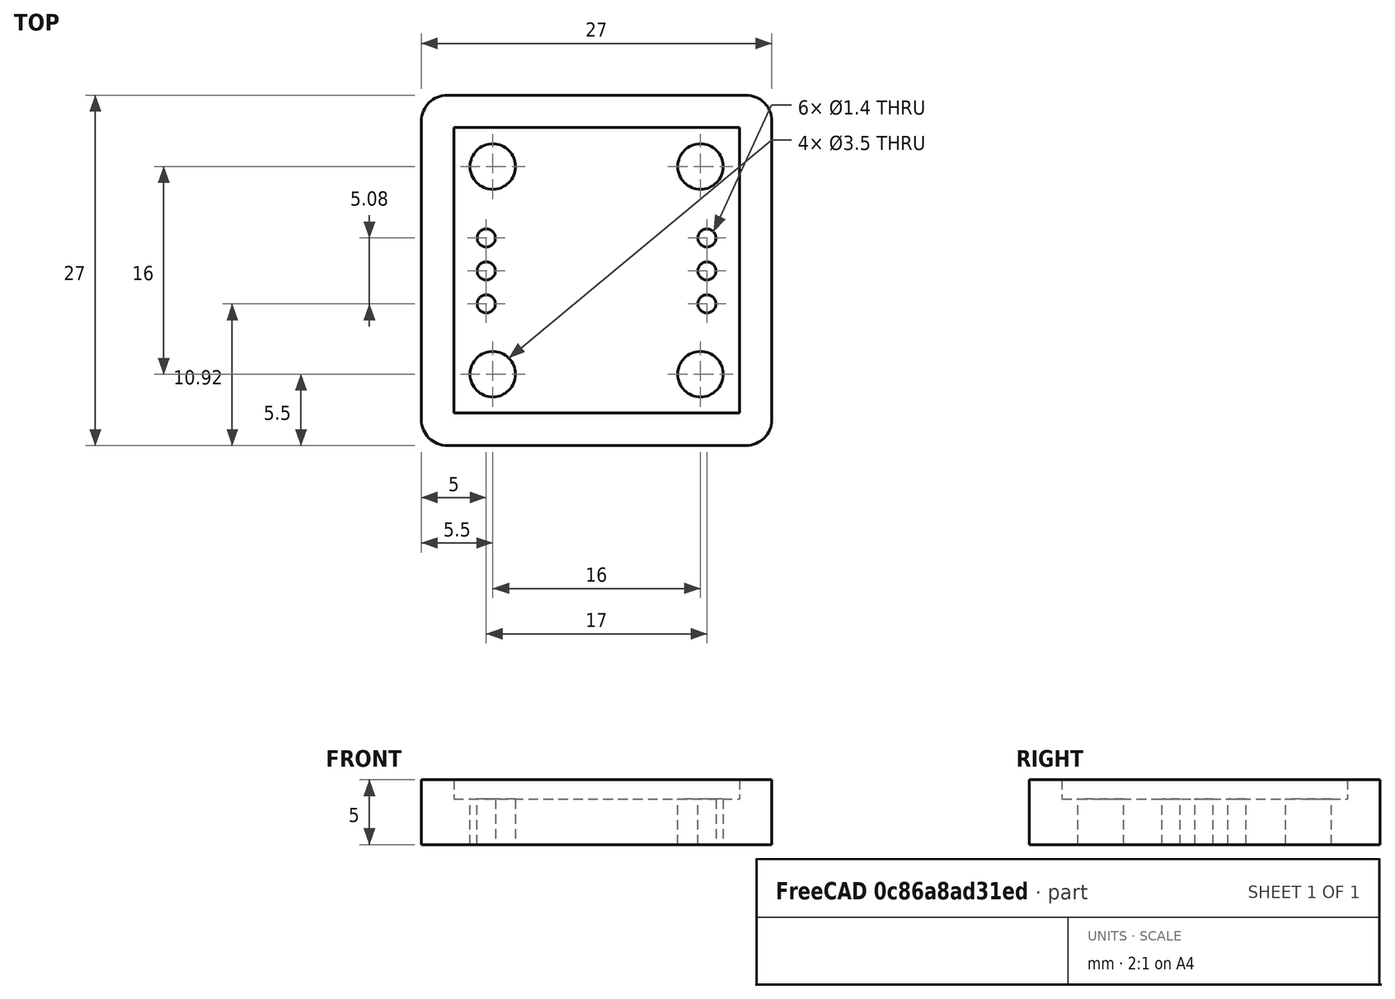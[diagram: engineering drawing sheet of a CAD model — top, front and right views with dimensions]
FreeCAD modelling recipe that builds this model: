
FCSTD DOCUMENT  (FreeCAD 1.1R44874 (Git))
Label: carrier1
Comment: Carrier for readout1
License: BSD 2-Clause
objects: Sketcher::SketchObject×4, PartDesign::Pocket×3, App::Point×1, PartDesign::Pad×1, PartDesign::Body×1, Mesh::Feature×1
note: 21 computed .brp shape members not serialized (recipe doc carries the construction recipe); baked Part::Feature solids carry a one-line shape summary decoded from their .brp

FEATURE [App::Point] Origin001
  Role = Origin
FEATURE [Sketcher::SketchObject] Sketch
  ArcFitTolerance = 1e-06
  AttachmentSupport = -> [Origin]
  ExternalTypes = [0]
  FullyConstrained = true
  MakeInternals = false
  MapMode = 5
  _ExternalGeoVersion = 1
  expr: Constraints[27] = .Constraints.outer - 2 * .Constraints.outerfilletradius
  sketch-geometry (13):
    g0: LineSegment StartX=-11.5 StartY=-13.5 StartZ=0 EndX=11.5 EndY=-13.5 EndZ=0
    g1: LineSegment StartX=13.5 StartY=-11.5 StartZ=0 EndX=13.5 EndY=11.5 EndZ=0
    g2: LineSegment StartX=11.5 StartY=13.5 StartZ=0 EndX=-11.5 EndY=13.5 EndZ=0
    g3: LineSegment StartX=-13.5 StartY=11.5 StartZ=0 EndX=-13.5 EndY=-11.5 EndZ=0
    g4: GeomPoint [constr] X=0 Y=0 Z=0
    g5: ArcOfCircle CenterX=-11.5 CenterY=11.5 CenterZ=0 NormalX=0 NormalY=0 NormalZ=1 AngleXU=0 Radius=2 StartAngle=1.5708 EndAngle=3.14159
    g6: GeomPoint [constr] X=-13.5 Y=13.5 Z=0
    g7: ArcOfCircle CenterX=-11.5 CenterY=-11.5 CenterZ=0 NormalX=0 NormalY=0 NormalZ=1 AngleXU=0 Radius=2 StartAngle=3.14159 EndAngle=4.71239
    g8: GeomPoint [constr] X=-13.5 Y=-13.5 Z=0
    g9: ArcOfCircle CenterX=11.5 CenterY=-11.5 CenterZ=0 NormalX=0 NormalY=0 NormalZ=1 AngleXU=0 Radius=2 StartAngle=4.71239 EndAngle=6.28319
    g10: GeomPoint [constr] X=13.5 Y=-13.5 Z=0
    g11: ArcOfCircle CenterX=11.5 CenterY=11.5 CenterZ=0 NormalX=0 NormalY=0 NormalZ=1 AngleXU=0 Radius=2 StartAngle=0 EndAngle=1.5708
    g12: GeomPoint [constr] X=13.5 Y=13.5 Z=0
  constraints (28):
    c: Horizontal(g0)
    c: Horizontal(g2)
    c: Vertical(g1)
    c: Vertical(g3)
    c: Symmetric(g12,g8,g4)
    c: Coincident(g4,g-1)
    c: DistanceX(g6,g12) = 27  'outer'
    c: PointOnObject(g6,g2)
    c: PointOnObject(g6,g3)
    c: Tangent(g2,g5) = -1.5708
    c: Tangent(g3,g5) = -1.5708
    c: PointOnObject(g8,g3)
    c: PointOnObject(g8,g0)
    c: Tangent(g3,g7) = -1.5708
    c: Tangent(g0,g7) = -1.5708
    c: PointOnObject(g10,g0)
    c: PointOnObject(g10,g1)
    c: Tangent(g0,g9) = -1.5708
    c: Tangent(g1,g9) = -1.5708
    c: PointOnObject(g12,g1)
    c: PointOnObject(g12,g2)
    c: Tangent(g1,g11) = -1.5708
    c: Tangent(g2,g11) = -1.5708
    c: Radius(g11) = 2  'outerfilletradius'
    c: Equal(g2,g3)
    c: Equal(g3,g0)
    c: Equal(g0,g1)
    c: DistanceX(g2,g2) = 23
FEATURE [PartDesign::Pad] Pad
  Direction = (0,0,1)
  Length = 5
  Length2 = 10
  Profile = -> Sketch
  ReferenceAxis = -> Sketch [N_Axis]
  Refine = true
  SideType = 0
  Suppressed = false
  Type = 0
  Type2 = 0
FEATURE [Sketcher::SketchObject] Sketch001
  ArcFitTolerance = 1e-06
  AttachmentSupport = -> [Pad]
  ExternalTypes = [0]
  FullyConstrained = true
  MakeInternals = false
  MapMode = 5
  Placement = pos=(0,0,5) rot=(0,0,1;0rad)
  _ExternalGeoVersion = 1
  sketch-geometry (5):
    g0: LineSegment StartX=-11 StartY=-11 StartZ=0 EndX=11 EndY=-11 EndZ=0
    g1: LineSegment StartX=11 StartY=-11 StartZ=0 EndX=11 EndY=11 EndZ=0
    g2: LineSegment StartX=11 StartY=11 StartZ=0 EndX=-11 EndY=11 EndZ=0
    g3: LineSegment StartX=-11 StartY=11 StartZ=0 EndX=-11 EndY=-11 EndZ=0
    g4: GeomPoint [constr] X=0 Y=0 Z=0
  constraints (12):
    c: Coincident(g0,g1)
    c: Coincident(g1,g2)
    c: Coincident(g2,g3)
    c: Coincident(g3,g0)
    c: Horizontal(g0)
    c: Horizontal(g2)
    c: Vertical(g1)
    c: Vertical(g3)
    c: Symmetric(g2,g0,g4)
    c: Coincident(g4,g-1)
    c: DistanceX(g2,g2) = 22  'outerpcb'
    c: Equal(g2,g3)
FEATURE [PartDesign::Pocket] Pocket  label="PCBPocket"
  BaseFeature = -> Pad
  Direction = (0,0,-1)
  Length = 1.5
  Length2 = 5
  Profile = -> Sketch001
  ReferenceAxis = -> Sketch001 [N_Axis]
  Refine = true
  SideType = 0
  Suppressed = false
  Type = 0
  Type2 = 0
FEATURE [Sketcher::SketchObject] Sketch002  label="mtgholes"
  ArcFitTolerance = 1e-06
  AttachmentSupport = -> [Pocket]
  ExternalTypes = [0]
  FullyConstrained = true
  MakeInternals = false
  MapMode = 5
  Placement = pos=(0,0,3.5) rot=(0,0,1;0rad)
  _ExternalGeoVersion = 1
  sketch-geometry (4):
    g0: Circle CenterX=8 CenterY=8 CenterZ=0 NormalX=0 NormalY=0 NormalZ=1 AngleXU=0 Radius=1.75
    g1: Circle CenterX=-8 CenterY=8 CenterZ=0 NormalX=0 NormalY=0 NormalZ=1 AngleXU=0 Radius=1.75
    g2: Circle CenterX=-8 CenterY=-8 CenterZ=0 NormalX=0 NormalY=0 NormalZ=1 AngleXU=0 Radius=1.75
    g3: Circle CenterX=8 CenterY=-8 CenterZ=0 NormalX=0 NormalY=0 NormalZ=1 AngleXU=0 Radius=1.75
  constraints (9):
    c: DistanceX(g-1,g0) = 8  'mtgholex'
    c: DistanceY(g-1,g0) = 8  'mtgholey'
    c: Equal(g0,g1)
    c: Equal(g0,g2)
    c: Equal(g0,g3)
    c: Symmetric(g1,g0,g-2)
    c: Symmetric(g3,g0,g-1)
    c: Symmetric(g2,g0,g-1)
    c: Diameter(g0) = 3.5  'mtgholedia'
FEATURE [PartDesign::Pocket] Pocket001
  BaseFeature = -> Pocket
  Direction = (0,0,-1)
  Length = 5
  Length2 = 5
  Profile = -> Sketch002
  ReferenceAxis = -> Sketch002 [N_Axis]
  Refine = true
  SideType = 0
  Suppressed = false
  Type = 2
  Type2 = 0
FEATURE [Sketcher::SketchObject] Sketch003
  ArcFitTolerance = 1e-06
  AttachmentSupport = -> [Pocket001]
  ExternalTypes = [0]
  FullyConstrained = true
  MakeInternals = false
  MapMode = 5
  Placement = pos=(0,0,3.5) rot=(0,0,1;0rad)
  _ExternalGeoVersion = 1
  sketch-geometry (6):
    g0: Circle CenterX=8.5 CenterY=2.5 CenterZ=0 NormalX=0 NormalY=0 NormalZ=1 AngleXU=0 Radius=0.7
    g1: Circle CenterX=8.5 CenterY=-0.04 CenterZ=0 NormalX=0 NormalY=0 NormalZ=1 AngleXU=0 Radius=0.7
    g2: Circle CenterX=8.5 CenterY=-2.58 CenterZ=0 NormalX=0 NormalY=0 NormalZ=1 AngleXU=0 Radius=0.7
    g3: Circle CenterX=-8.5 CenterY=2.5 CenterZ=0 NormalX=0 NormalY=0 NormalZ=1 AngleXU=0 Radius=0.7
    g4: Circle CenterX=-8.5 CenterY=-0.04 CenterZ=0 NormalX=0 NormalY=0 NormalZ=1 AngleXU=0 Radius=0.7
    g5: Circle CenterX=-8.5 CenterY=-2.58 CenterZ=0 NormalX=0 NormalY=0 NormalZ=1 AngleXU=0 Radius=0.7
  constraints (15):
    c: Diameter(g0) = 1.4  'pindia'
    c: DistanceX(g-1,g0) = 8.5  'pin1x'
    c: DistanceY(g-1,g0) = 2.5  'pin1y'
    c: Diameter(g4) = 1.4
    c: Equal(g5,g2)
    c: Equal(g2,g1)
    c: Symmetric(g5,g2,g-2)
    c: Symmetric(g4,g1,g-2)
    c: Symmetric(g3,g0,g-2)
    c: Equal(g4,g3)
    c: Equal(g1,g0)
    c: DistanceX(g-1,g2) = 8.5
    c: DistanceX(g-1,g1) = 8.5
    c: DistanceY(g2,g1) = 2.54
    c: DistanceY(g4,g3) = 2.54
FEATURE [PartDesign::Pocket] Pocket002
  BaseFeature = -> Pocket001
  Direction = (0,0,-1)
  Length = 5
  Length2 = 5
  Profile = -> Sketch003
  ReferenceAxis = -> Sketch003 [N_Axis]
  Refine = true
  SideType = 0
  Suppressed = false
  Type = 2
  Type2 = 0
FEATURE [PartDesign::Body] Body
  AllowCompound = true
  Group = -> [Sketch,Pad,Sketch001,Pocket,Sketch002,Pocket001,Sketch003,Pocket002]
  Origin = -> Origin
  Tip = -> Pocket002
FEATURE [Mesh::Feature] Mesh  label="Body (Meshed)"
